# Revit family: ArandelaConcreto_ASC5W_ASC10W_PowerLume
name_source: partatom
category: Luminárias
units: mm (PartAtom-declared; Revit-internal decimal feet)

## family parameters
Compartilhado = Sim
Corte com vazios quando carregada = Sim
Cota do conector redondo = Utilizar diâmetro
Fonte luminosa = Não
Hospedeiro = Face
Manter orientação da anotação = Não
Número OmniClass = 23.80.70.14.11.17
Ponto de cálculo do ambiente = Não
Tipo de parte = Normal
Título OmniClass = Wall or Ceiling Mounted External Lighting

## types (2) — shared parameters
Base = Metal - Alumínio
Carga Aparente Luminária = 0 VA
Catálogo de produtos = https://www.powerlume.com.br
Comentários de voltagem = 110 ou 220Vac 50/60Hz com driver incorporado
Contato do fabricante = (54) 3066-6488
Data da atualização = 27/02/2025
Descrição = Arandela de sobrepor LED indireta em concreto
Difusor = PMMA injetado leitoso anti UV
Elevação-padrão = 1219 mm
Fabricante = Power Lume
Fator de Potência Luminária = 1
Frame = Concreto, leve
IP = 65
IRC = 85
IfcExportAs = IfcLightFixtureType
Localização = Caxias do Sul - RS / Brasil
Lâmpada = Placa LED
Peso = 0
Temperatura de cor = 3000K
Tipo de imagem = FOTO ASC5W ASC10W.png
URL = https://www.powerlume.com.br
URL do produto = https://www.powerlume.com.br
Versão = 1
Vida útil = 60000h
Voltagem Luminária = 0 V
Ângulo de abertura = Difuso indireto

## per-type parameters (varying)
| type | Altura | Diâmetro do frame | Fluxo luminoso | Modelo de luminária | Potência |
| ASC5W | 70 mm  [stored 0.229659 ft] | 200 mm  [stored 0.656168 ft] | 800 lm | ArandelaConcreto_ASC5W_Base_PowerLume : ASC5W | 5W |
| ASC10W | 95 mm | 285 mm  [stored 0.935039 ft] | 1400 lm | ArandelaConcreto_ASC10W_Base_PowerLume : ASC10W | 10W |

note: column(s) folded — value = type name in every type: Modelo

note: [stored X ft] marks values corroborated as IEEE doubles in the binary element streams (Revit-internal decimal feet)
